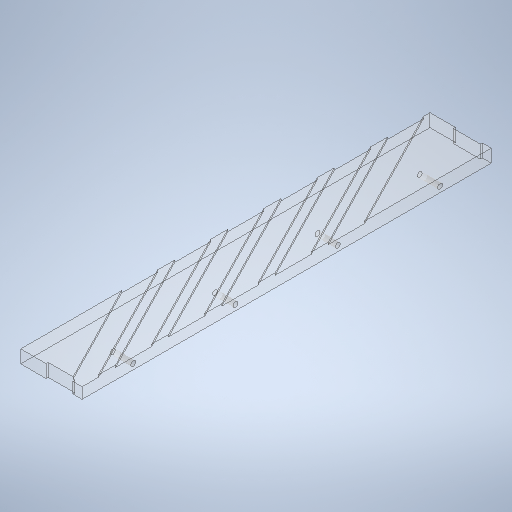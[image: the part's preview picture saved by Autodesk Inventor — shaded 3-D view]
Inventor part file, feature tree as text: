
AUTODESK INVENTOR PART (.ipt)
format: ipt  version: 2025 (Build 290162000, 162)  size: 361,984 bytes
history: native  units: in
note: dims shown in document units (in); Inventor stores cm internally (conversion verified against a paired STEP export)
features: sketch x6, extrude x4, hole x1
ambient origin geometry x8: Origin, YZ Plane, XZ Plane, XY Plane, X Axis, Y Axis, Z Axis, Center Point
bodies: Body1 (feature_tree)
feature tree (11):
  extrude  "Extrusion2"  Depth=7.874in
  extrude  "Extrusion3"  Depth=0.25in
  extrude  "Extrusion5"  Depth=0.0394in TaperAngle=0.0deg
  extrude  "Extrusion6"  Depth=0.3937in
  hole  "Hole1"  [1 undecoded]
  sketch  "Sketch3"  dims[d9=0.25in d10=0.0in d11=0.1855in]
  sketch  "Sketch4"  dims[d12=0.315in d14=0.0394in d15=0.0in]
  sketch  "Sketch Rectangular Pattern1"  dims[d7=1.1811in d8=7.874in]
  sketch  "Sketch7"  dims[d23=0.315in d24=2.3622in d26=1.0236in d27=0.3937in d29=0.3937in]
  sketch  "Sketch8"  dims[d40=0.1772in d41=0.689in]
  sketch  "Sketch9"  dims[d42=0.0394in d43=0.0in d44=0.1772in d45=0.689in d46=0.0394in d47=0.0in d48=0.1053in d49=0.9843in d50=1.9685in d51=0.9843in d52=1.9685in d53=0.0968in d54=0.2953in d55=0.1575in d56=0.0787in d57=90.0deg d58=0.3937in d59=0.8108in]
note: 1 required parameter value undecoded (feature->parameter linkage not recoverable at this tier; creation-order binding heuristic only, values carry confidence <= 0.55)
